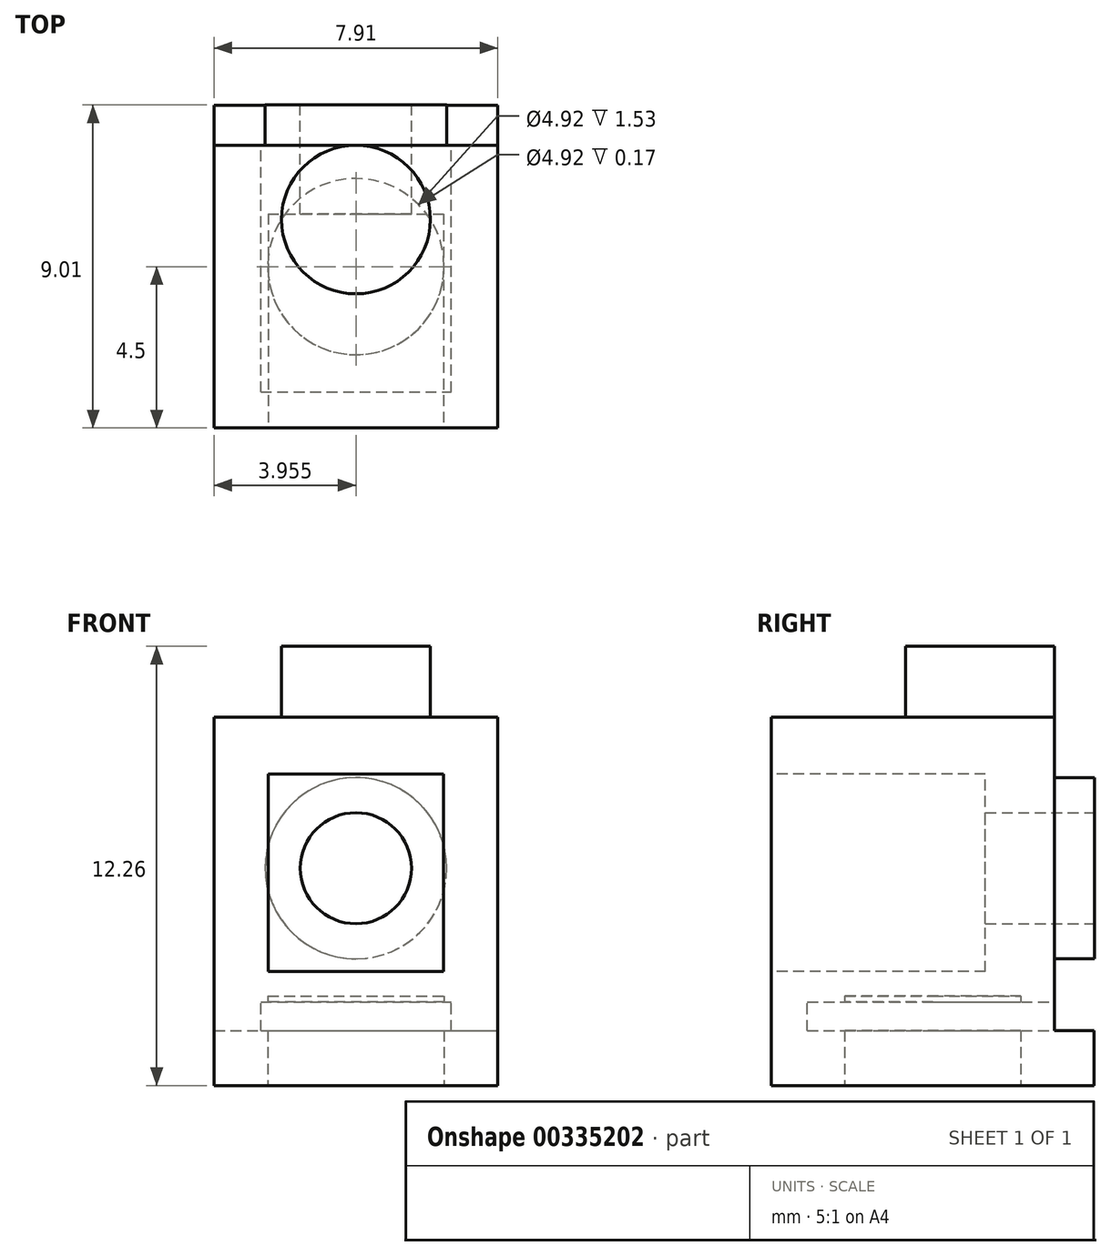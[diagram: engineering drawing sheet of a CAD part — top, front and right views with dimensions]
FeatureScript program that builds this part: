
annotation { "Feature Type Name" : "Feature", "Feature Type Description" : "" }
export const myFeature = defineFeature(function(context is Context, id is Id, definition is map)
    precondition{}
    {
        {
            var Q0;
            Q0=qCreatedBy(makeId("Front.planeOp"),FACE);
            var sketch = newSketch(context, id + "F0", { "sketchPlane" : qUnion([Q0])});
            skLineSegment(sketch, "E0", {"start": v(0, 0) * mm, "end": v(0, 10.28) * mm});
            skLineSegment(sketch, "E1", {"start": v(0, 10.28) * mm, "end": v(7.9, 10.28) * mm});
            skLineSegment(sketch, "E2", {"start": v(7.9, 10.28) * mm, "end": v(7.9, 0) * mm});
            skLineSegment(sketch, "E3", {"start": v(7.9, 0) * mm, "end": v(0, 0) * mm});
            skLineSegment(sketch, "E4", {"start": v(0, 1.53) * mm, "end": v(7.9, 1.53) * mm});
            skLineSegment(sketch, "E5.bottom", {"start": v(1.3, 1.53) * mm, "end": v(6.6, 1.53) * mm});
            skLineSegment(sketch, "E5.top", {"start": v(1.3, 2.33) * mm, "end": v(6.6, 2.33) * mm});
            skLineSegment(sketch, "E5.left", {"start": v(1.3, 1.53) * mm, "end": v(1.3, 2.33) * mm});
            skLineSegment(sketch, "E5.right", {"start": v(6.6, 1.53) * mm, "end": v(6.6, 2.33) * mm});
            skSolve(sketch);
        }
        {
            var Q0;
            {var subQ1=sQuery(id+"F0.wireOp",EDGE,"E1");Q0=makeQuery(id+"F0.imprint","IMPRINT",FACE,{"disambiguationData":[TD([[makeQuery(id+"F0.imprint","IMPRINT",EDGE,{"derivedFrom":subQ1}),-1.0]])]});}
            extrude(context, id + "F1", {"entities" : qUnion([Q0]), "depth" : 7.89 * mm});
        }
        {
            var Q0;
            Q0=makeQuery(id+"F1.opExtrude","CAP_FACE",FACE,{"disambiguationData":[OSD([sQuery(id+"F0.wireOp",EDGE,"E0"),sQuery(id+"F0.wireOp",EDGE,"E1"),sQuery(id+"F0.wireOp",EDGE,"E2"),sQuery(id+"F0.wireOp",EDGE,"E4"),sQuery(id+"F0.wireOp",EDGE,"E5.top"),sQuery(id+"F0.wireOp",EDGE,"E5.left"),sQuery(id+"F0.wireOp",EDGE,"E5.right")])],"isStart":false});
            var sketch = newSketch(context, id + "F2", { "sketchPlane" : qUnion([Q0])});
            skLineSegment(sketch, "E6", {"start": v(0, 1.53) * mm, "end": v(0, 0) * mm});
            skLineSegment(sketch, "E7", {"start": v(0, 0) * mm, "end": v(7.9, 0) * mm});
            skLineSegment(sketch, "E8", {"start": v(7.9, 0) * mm, "end": v(7.9, 1.53) * mm});
            skLineSegment(sketch, "E9", {"start": v(1.3, 1.53) * mm, "end": v(6.6, 1.53) * mm});
            skSolve(sketch);
        }
        {
            var Q0;
            Q0 = qSketchRegion(id + "F2", true);
            var Q1;
            Q1=makeQuery(id+"F2.imprint","IMPRINT",FACE,{"disambiguationData":[TD([[makeQuery(id+"F2.imprint","IMPRINT",EDGE,{"derivedFrom":sQuery(id+"F2.wireOp",EDGE,"E6")}),1.0]])]});
            extrude(context, id + "F3", {"entities" : qUnion([Q0, Q1]), "operationType" : NewBodyOperationType.ADD, "oppositeDirection" : true, "depth" : 9 * mm});
        }
        {
            var Q0;
            Q0=makeQuery(id+"F1.opExtrude","CAP_FACE",FACE,{"disambiguationData":[OSD([sQuery(id+"F0.wireOp",EDGE,"E0"),sQuery(id+"F0.wireOp",EDGE,"E1"),sQuery(id+"F0.wireOp",EDGE,"E2"),sQuery(id+"F0.wireOp",EDGE,"E4"),sQuery(id+"F0.wireOp",EDGE,"E5.top"),sQuery(id+"F0.wireOp",EDGE,"E5.left"),sQuery(id+"F0.wireOp",EDGE,"E5.right")])],"isStart":true});
            var sketch = newSketch(context, id + "F4", { "sketchPlane" : qUnion([Q0])});
            skCircle(sketch, "E10", {"center": v(-3.96, 6.07) * mm, "radius": 1.55 * mm});
            skCircle(sketch, "E11", {"center": v(-3.96, 6.07) * mm, "radius": 1.98 * mm});
            skSolve(sketch);
        }
        {
            var Q0;
            Q0=makeQuery(id+"F4.imprint","IMPRINT",FACE,{"disambiguationData":[TD([[makeQuery(id+"F4.imprint","IMPRINT",EDGE,{"derivedFrom":sQuery(id+"F4.wireOp",EDGE,"E10")}),1.0]])]});
            extrude(context, id + "F5", {"entities" : qUnion([Q0]), "operationType" : NewBodyOperationType.ADD, "depth" : 25 * mm});
        }
        {
            var Q0;
            Q0=makeQuery(id+"F5.opExtrude","CAP_FACE",FACE,{"disambiguationData":[OSD([sQuery(id+"F4.wireOp",EDGE,"E10")])],"isStart":false});
            extrude(context, id + "F6", {"entities" : qUnion([Q0]), "operationType" : NewBodyOperationType.REMOVE, "oppositeDirection" : true, "depth" : 33 * mm});
        }
        {
            var Q0;
            Q0=makeQuery(id+"F1.opExtrude","CAP_FACE",FACE,{"disambiguationData":[OSD([sQuery(id+"F0.wireOp",EDGE,"E0"),sQuery(id+"F0.wireOp",EDGE,"E1"),sQuery(id+"F0.wireOp",EDGE,"E2"),sQuery(id+"F0.wireOp",EDGE,"E4"),sQuery(id+"F0.wireOp",EDGE,"E5.top"),sQuery(id+"F0.wireOp",EDGE,"E5.left"),sQuery(id+"F0.wireOp",EDGE,"E5.right")])],"isStart":true});
            var sketch = newSketch(context, id + "F7", { "sketchPlane" : qUnion([Q0])});
            skCircle(sketch, "E12", {"center": v(-3.96, 6.07) * mm, "radius": 2.53 * mm});
            skSolve(sketch);
        }
        {
            var Q0;
            Q0=makeQuery(id+"F7.imprint","IMPRINT",FACE,{"disambiguationData":[TD([[makeQuery(id+"F7.imprint","IMPRINT",EDGE,{"derivedFrom":sQuery(id+"F7.wireOp",EDGE,"E12")}),1.0]])]});
            extrude(context, id + "F8", {"entities" : qUnion([Q0]), "operationType" : NewBodyOperationType.ADD, "depth" : 1.12 * mm});
        }
        {
            var Q0;
            Q0=makeQuery(id+"F1.opExtrude","SWEPT_FACE",FACE,{"disambiguationData":[OSD([sQuery(id+"F0.wireOp",EDGE,"E1")])]});
            var sketch = newSketch(context, id + "F9", { "sketchPlane" : qUnion([Q0])});
            skCircle(sketch, "E13", {"center": v(3.96, -2.08) * mm, "radius": 2.08 * mm});
            skSolve(sketch);
        }
        {
            var Q0;
            Q0=makeQuery(id+"F9.imprint","IMPRINT",FACE,{"disambiguationData":[TD([[makeQuery(id+"F9.imprint","IMPRINT",EDGE,{"derivedFrom":sQuery(id+"F9.wireOp",EDGE,"E13")}),1.0]])]});
            extrude(context, id + "F10", {"entities" : qUnion([Q0]), "operationType" : NewBodyOperationType.ADD, "depth" : 1.98 * mm});
        }
        {
            var Q0;
            {var subQ0=sQuery(id+"F0.wireOp",EDGE,"E4");Q0=makeQuery(id+"F3.boolean.opBoolean","MERGE",FACE,{"derivedFrom":[makeQuery(id+"F1.opExtrude","CAP_FACE",FACE,{"disambiguationData":[OSD([sQuery(id+"F0.wireOp",EDGE,"E0"),sQuery(id+"F0.wireOp",EDGE,"E1"),sQuery(id+"F0.wireOp",EDGE,"E2"),subQ0,sQuery(id+"F0.wireOp",EDGE,"E5.top"),sQuery(id+"F0.wireOp",EDGE,"E5.left"),sQuery(id+"F0.wireOp",EDGE,"E5.right")])],"isStart":false}),makeQuery(id+"F3.opExtrude","CAP_FACE",FACE,{"disambiguationData":[OSD([subQ0,sQuery(id+"F2.wireOp",EDGE,"E6"),sQuery(id+"F2.wireOp",EDGE,"E7"),sQuery(id+"F2.wireOp",EDGE,"E8"),sQuery(id+"F2.wireOp",EDGE,"E9")])],"isStart":true})]});}
            var sketch = newSketch(context, id + "F11", { "sketchPlane" : qUnion([Q0])});
            skLineSegment(sketch, "E14", {"start": v(1.3, 1.53) * mm, "end": v(1.3, 2.33) * mm});
            skLineSegment(sketch, "E15", {"start": v(1.3, 2.33) * mm, "end": v(6.6, 2.33) * mm});
            skLineSegment(sketch, "E16", {"start": v(6.6, 2.33) * mm, "end": v(6.6, 1.53) * mm});
            skLineSegment(sketch, "E17", {"start": v(6.6, 1.53) * mm, "end": v(1.3, 1.53) * mm});
            skSolve(sketch);
        }
        {
            var Q0;
            Q0=makeQuery(id+"F11.imprint","IMPRINT",FACE,{"disambiguationData":[TD([[makeQuery(id+"F11.imprint","IMPRINT",EDGE,{"derivedFrom":sQuery(id+"F11.wireOp",EDGE,"E14")}),-1.0]])]});
            extrude(context, id + "F12", {"entities" : qUnion([Q0]), "operationType" : NewBodyOperationType.ADD, "oppositeDirection" : true, "depth" : 1 * mm});
        }
        {
            var Q0;
            {var subQ0=sQuery(id+"F0.wireOp",EDGE,"E4");Q0=makeQuery(id+"F12.boolean.opBoolean","MERGE",FACE,{"derivedFrom":[makeQuery(id+"F3.boolean.opBoolean","MERGE",FACE,{"derivedFrom":[makeQuery(id+"F1.opExtrude","CAP_FACE",FACE,{"disambiguationData":[OSD([sQuery(id+"F0.wireOp",EDGE,"E0"),sQuery(id+"F0.wireOp",EDGE,"E1"),sQuery(id+"F0.wireOp",EDGE,"E2"),subQ0,sQuery(id+"F0.wireOp",EDGE,"E5.top"),sQuery(id+"F0.wireOp",EDGE,"E5.left"),sQuery(id+"F0.wireOp",EDGE,"E5.right")])],"isStart":false}),makeQuery(id+"F3.opExtrude","CAP_FACE",FACE,{"disambiguationData":[OSD([subQ0,sQuery(id+"F2.wireOp",EDGE,"E6"),sQuery(id+"F2.wireOp",EDGE,"E7"),sQuery(id+"F2.wireOp",EDGE,"E8"),sQuery(id+"F2.wireOp",EDGE,"E9")])],"isStart":true})]}),makeQuery(id+"F12.opExtrude","CAP_FACE",FACE,{"disambiguationData":[OSD([sQuery(id+"F11.wireOp",EDGE,"E14"),sQuery(id+"F11.wireOp",EDGE,"E15"),sQuery(id+"F11.wireOp",EDGE,"E16"),sQuery(id+"F11.wireOp",EDGE,"E17")])],"isStart":true})]});}
            var sketch = newSketch(context, id + "F13", { "sketchPlane" : qUnion([Q0])});
            skLineSegment(sketch, "E18.bottom", {"start": v(1.5, 8.7) * mm, "end": v(6.4, 8.7) * mm});
            skLineSegment(sketch, "E18.top", {"start": v(1.5, 3.18) * mm, "end": v(6.4, 3.18) * mm});
            skLineSegment(sketch, "E19", {"start": v(1.5, 3.18) * mm, "end": v(1.5, 8.7) * mm});
            skLineSegment(sketch, "E20", {"start": v(6.4, 3.18) * mm, "end": v(6.4, 8.7) * mm});
            skSolve(sketch);
        }
        {
            var Q0;
            Q0 = qSketchRegion(id + "F13", true);
            extrude(context, id + "F14", {"entities" : qUnion([Q0]), "operationType" : NewBodyOperationType.REMOVE, "oppositeDirection" : true, "depth" : 5.97 * mm});
        }
        {
            var Q0;
            Q0=makeQuery(id+"F3.opExtrude","SWEPT_FACE",FACE,{"disambiguationData":[OSD([sQuery(id+"F2.wireOp",EDGE,"E7")])]});
            var sketch = newSketch(context, id + "F15", { "sketchPlane" : qUnion([Q0])});
            skCircle(sketch, "E21", {"center": v(3.96, 3.39) * mm, "radius": 2.46 * mm});
            skSolve(sketch);
        }
        {
            var Q0;
            Q0 = qSketchRegion(id + "F15", true);
            extrude(context, id + "F16", {"entities" : qUnion([Q0]), "operationType" : NewBodyOperationType.REMOVE, "oppositeDirection" : true, "depth" : 2.5 * mm});
        }
    });
